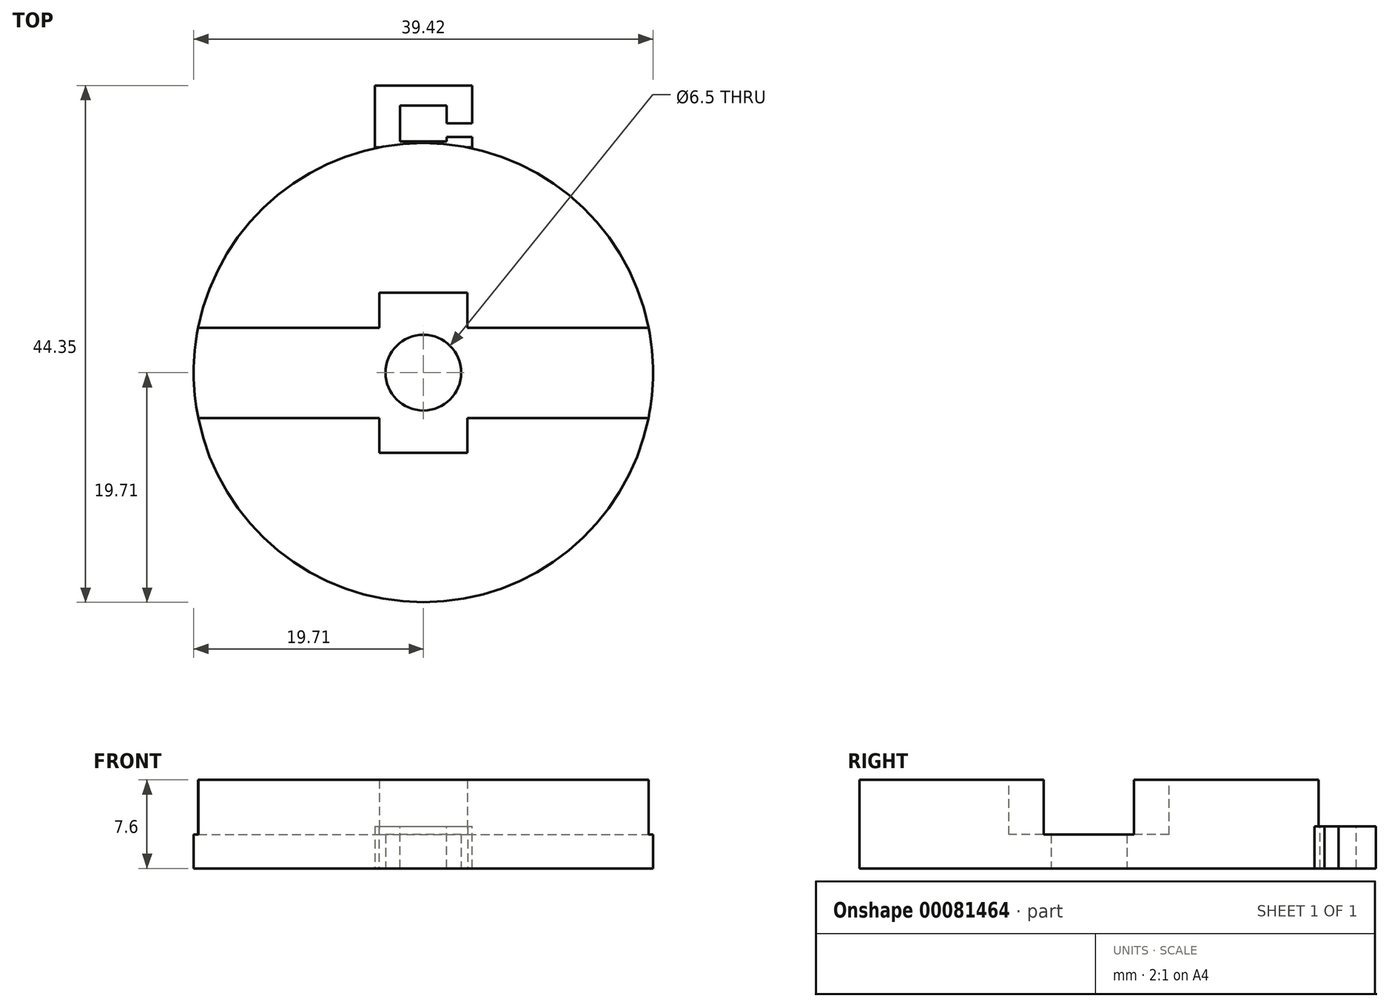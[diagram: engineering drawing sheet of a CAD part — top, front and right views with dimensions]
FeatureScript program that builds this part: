
annotation { "Feature Type Name" : "Feature", "Feature Type Description" : "" }
export const myFeature = defineFeature(function(context is Context, id is Id, definition is map)
    precondition{}
    {
        {
            var Q0;
            Q0=qCreatedBy(makeId("Top.planeOp"),FACE);
            var sketch = newSketch(context, id + "F0", { "sketchPlane" : qUnion([Q0])});
            skCircle(sketch, "E0", {"center": v(0, 0) * mm, "radius": 19.71 * mm});
            skSolve(sketch);
        }
        {
            var Q0;
            Q0 = qSketchRegion(id + "F0", true);
            extrude(context, id + "F1", {"entities" : qUnion([Q0]), "depth" : 7.6 * mm});
        }
        {
            var Q0;
            Q0=makeQuery(id+"F1.opExtrude","CAP_FACE",FACE,{"disambiguationData":[OSD([sQuery(id+"F0.wireOp",EDGE,"E0")])],"isStart":false});
            var sketch = newSketch(context, id + "F2", { "sketchPlane" : qUnion([Q0])});
            skLineSegment(sketch, "E1.bottom", {"start": v(-20, 3.85) * mm, "end": v(20, 3.85) * mm});
            skLineSegment(sketch, "E1.top", {"start": v(-20, -3.9) * mm, "end": v(20, -3.9) * mm});
            skLineSegment(sketch, "E1.left", {"start": v(-20, 3.85) * mm, "end": v(-20, -3.9) * mm});
            skLineSegment(sketch, "E1.right", {"start": v(20, 3.85) * mm, "end": v(20, -3.9) * mm});
            skSolve(sketch);
        }
        {
            var Q0;
            Q0 = qSketchRegion(id + "F2", true);
            extrude(context, id + "F3", {"entities" : qUnion([Q0]), "operationType" : NewBodyOperationType.REMOVE, "oppositeDirection" : true, "depth" : 4.7 * mm});
        }
        {
            var Q0;
            {var subQ0=sQuery(id+"F0.wireOp",EDGE,"E0");Q0=makeQuery(id+"F3.boolean.opBoolean","SPLIT",FACE,{"disambiguationData":[TD([makeQuery(id+"F3.opExtrude","SWEPT_FACE",FACE,{"disambiguationData":[OSD([sQuery(id+"F2.wireOp",EDGE,"E1.bottom")])]})])],"derivedFrom":makeQuery(id+"F1.opExtrude","CAP_FACE",FACE,{"disambiguationData":[OSD([subQ0])],"isStart":false})});}
            var sketch = newSketch(context, id + "F4", { "sketchPlane" : qUnion([Q0])});
            skLineSegment(sketch, "E2.bottom", {"start": v(-3.78, 6.88) * mm, "end": v(3.78, 6.88) * mm});
            skLineSegment(sketch, "E2.top", {"start": v(-3.78, -6.88) * mm, "end": v(3.78, -6.88) * mm});
            skLineSegment(sketch, "E2.left", {"start": v(-3.78, 6.88) * mm, "end": v(-3.78, -6.88) * mm});
            skLineSegment(sketch, "E2.right", {"start": v(3.77, 6.88) * mm, "end": v(3.78, -6.88) * mm});
            skSolve(sketch);
        }
        {
            var Q0;
            Q0 = qSketchRegion(id + "F4", true);
            extrude(context, id + "F5", {"entities" : qUnion([Q0]), "operationType" : NewBodyOperationType.REMOVE, "oppositeDirection" : true, "depth" : 4.7 * mm});
        }
        {
            var Q0;
            Q0=makeQuery(id+"F1.opExtrude","CAP_FACE",FACE,{"disambiguationData":[OSD([sQuery(id+"F0.wireOp",EDGE,"E0")])],"isStart":true});
            var sketch = newSketch(context, id + "F6", { "sketchPlane" : qUnion([Q0])});
            skLineSegment(sketch, "E3.bottom", {"start": v(-4.18, -19.34) * mm, "end": v(4.17, -19.34) * mm});
            skLineSegment(sketch, "E3.top", {"start": v(-4.18, -24.64) * mm, "end": v(4.18, -24.64) * mm});
            skLineSegment(sketch, "E3.left", {"start": v(-4.18, -19.34) * mm, "end": v(-4.18, -24.64) * mm});
            skLineSegment(sketch, "E3.right", {"start": v(4.17, -19.34) * mm, "end": v(4.17, -24.64) * mm});
            skSolve(sketch);
        }
        {
            var Q0;
            Q0 = qSketchRegion(id + "F6", true);
            extrude(context, id + "F7", {"entities" : qUnion([Q0]), "operationType" : NewBodyOperationType.ADD, "oppositeDirection" : true, "depth" : 3.6 * mm});
        }
        {
            var Q0;
            Q0=makeQuery(id+"F7.opExtrude","CAP_FACE",FACE,{"disambiguationData":[OSD([sQuery(id+"F6.wireOp",EDGE,"E3.bottom"),sQuery(id+"F6.wireOp",EDGE,"E3.top"),sQuery(id+"F6.wireOp",EDGE,"E3.left"),sQuery(id+"F6.wireOp",EDGE,"E3.right")])],"isStart":false});
            var sketch = newSketch(context, id + "F8", { "sketchPlane" : qUnion([Q0])});
            skLineSegment(sketch, "E4.bottom", {"start": v(-2, 22.94) * mm, "end": v(2, 22.94) * mm});
            skLineSegment(sketch, "E4.top", {"start": v(-2, 19.84) * mm, "end": v(2, 19.84) * mm});
            skLineSegment(sketch, "E4.left", {"start": v(-2, 22.94) * mm, "end": v(-2, 19.84) * mm});
            skLineSegment(sketch, "E4.right", {"start": v(2, 22.94) * mm, "end": v(2, 19.84) * mm});
            skLineSegment(sketch, "E5.bottom", {"start": v(2, 21.42) * mm, "end": v(4.17, 21.42) * mm});
            skLineSegment(sketch, "E5.top", {"start": v(2, 20.22) * mm, "end": v(4.17, 20.22) * mm});
            skLineSegment(sketch, "E5.left", {"start": v(2, 21.42) * mm, "end": v(2, 20.22) * mm});
            skLineSegment(sketch, "E5.right", {"start": v(4.17, 21.42) * mm, "end": v(4.17, 20.22) * mm});
            skSolve(sketch);
        }
        {
            var Q0;
            Q0 = qSketchRegion(id + "F8", true);
            extrude(context, id + "F9", {"entities" : qUnion([Q0]), "operationType" : NewBodyOperationType.REMOVE, "endBound" : BoundingType.THROUGH_ALL, "oppositeDirection" : true, "depth" : 25 * mm});
        }
        {
            var Q0;
            Q0=makeQuery(id+"F7.boolean.opBoolean","MERGE",FACE,{"derivedFrom":[makeQuery(id+"F1.opExtrude","CAP_FACE",FACE,{"disambiguationData":[OSD([sQuery(id+"F0.wireOp",EDGE,"E0")])],"isStart":true}),makeQuery(id+"F7.opExtrude","CAP_FACE",FACE,{"disambiguationData":[OSD([sQuery(id+"F6.wireOp",EDGE,"E3.bottom"),sQuery(id+"F6.wireOp",EDGE,"E3.top"),sQuery(id+"F6.wireOp",EDGE,"E3.left"),sQuery(id+"F6.wireOp",EDGE,"E3.right")])],"isStart":true})]});
            var sketch = newSketch(context, id + "F10", { "sketchPlane" : qUnion([Q0])});
            skCircle(sketch, "E6", {"center": v(0, 0) * mm, "radius": 3.25 * mm});
            skSolve(sketch);
        }
        {
            var Q0;
            Q0 = qSketchRegion(id + "F10", true);
            extrude(context, id + "F11", {"entities" : qUnion([Q0]), "operationType" : NewBodyOperationType.REMOVE, "oppositeDirection" : true, "depth" : 3 * mm});
        }
    });
